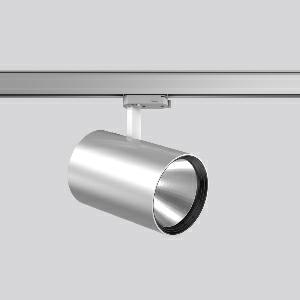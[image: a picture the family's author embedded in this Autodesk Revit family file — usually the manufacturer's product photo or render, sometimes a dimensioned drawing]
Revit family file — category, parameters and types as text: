
# Revit family: deecos_s_maxi_742211_004_9e86
name_source: partatom
category: Lighting Fixtures
units: mm (PartAtom-declared; Revit-internal decimal feet)

## family parameters
Cut with Voids When Loaded = No
Host = Face
Light Source = No
Part Type = Normal
Room Calculation Point = No
Round Connector Dimension = Use Diameter
Shared = No

## types (1)
- DEECOS S maxi (1 x LED Modul 930, 2250 lm, 3000)
    Apparent Load = 22 VA
    Approval mark = CE
    CIE Flux Codes = 100 100 100 100 100
    Color Rendering = 90
    Color Temperature = 3000
    Default Elevation = 1800 mm
    Description = Series: DEECOS S maxi
LED surface-mounted projector in modern design with no visible cooling ribs. Housing: die-cast aluminium, powder-coated. Rotation range: 356°. Swivel range: 90°. Black plastic ring and recessed LED to prevent glare from the side. Optical assembly with reflector made of MIRO-Silver with 98% total light reflection for outstanding efficiency - can be changed without tools. Best colour rendering index Ra>90. Superspot version with small spot LED. With multi adaptor for 3-circuit tracks 230 V. Suitable for Track on ceiling, Wall track. High quality converter without flickering and stroboscopic effect. The following accessories can be mounted without use of tools: interchangeable lenses, decorative glasses, honeycomb louvre, clear and frosted diffusers, white interchangeable plastic ring. 
Colour: silver
Diameter: 123 mm
Height: 200 mm
Lamp: LED
Socket: without socket
Colour temperature: 3000K
Colour rendering index (CRI): 92
System power: 22 W
Rated luminous flux: 2250 lm
Luminous efficiency: 102 lm/W
Control gear: Regulated power supply
Protection class: I
Type of protection: IP 20
    Height = 200 mm  [stored 0.656168 ft]
    Lamp = 1 x LED Modul 930
    Lamp Light Flux = 2250 lm
    Lamp count = 1
    Length = 123 mm
    Lifetime = 50000 h
    Luminous efficacy = 102 lm/W
    Manufacturer = RZB
    ModVariant = No
    Model = 742211.004
    Mounting Place = Ceiling
    Mounting Type = Rail mounted
    Number of Poles = 1
    OnlyDefault = Yes
    Power Factor = 1
    Product Name = DEECOS S maxi
    Product group = Track mounted projectors
    ProductGroupID = 301
    Protection Class = Protection class I
    Protection Degree = IP 20
    RLX_Detail_Level = 1
    RLX_Emergency_Light_Flux = 0 lm
    RLX_Emergency_Type = 0
    RLX_Emergency_Type_DB = No
    RlxData = <blob elided: 40429 chars, md5=a14cc504>
    Socket = socket
    Standby Power = 0 W
    System Light Flux = 2250 lm
    System Power = 22 W
    Type Comments = Product without accessories
    Type Image = 741954.004.jpg
    URL = http://relux.com
    VarID = ---
    Voltage = 230 V
    Voltage Range = 220-240 V
    Weight = 0.00 kg
    Width = 0 mm  [stored 0 ft]

note: [stored X ft] marks values corroborated as IEEE doubles in the binary element streams (Revit-internal decimal feet)

## geometry (parser evidence)
native form markers: Blend x4, Sweep x10
no freeform markers — native parametric forms only
